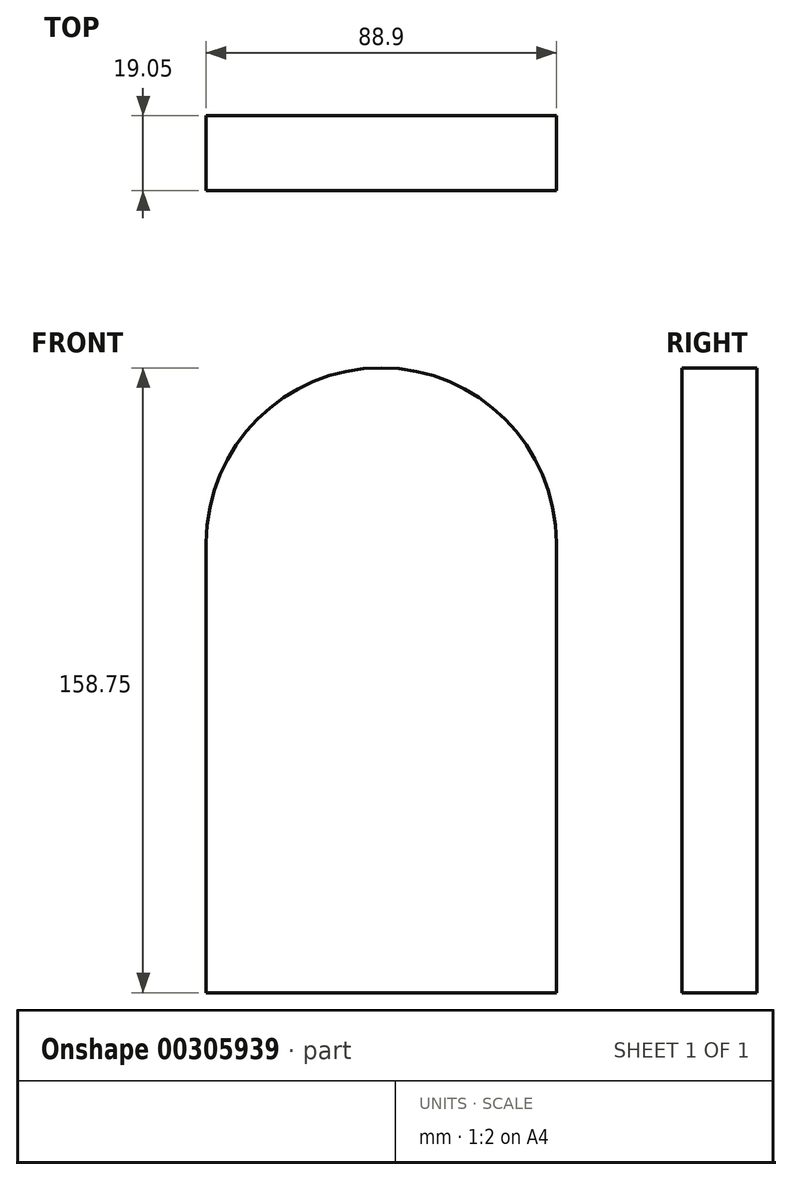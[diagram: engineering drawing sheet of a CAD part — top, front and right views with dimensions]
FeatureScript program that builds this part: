
annotation { "Feature Type Name" : "Feature", "Feature Type Description" : "" }
export const myFeature = defineFeature(function(context is Context, id is Id, definition is map)
    precondition{}
    {
        {
            var Q0;
            Q0=qCreatedBy(makeId("Front.planeOp"),FACE);
            var sketch = newSketch(context, id + "F0", { "sketchPlane" : qUnion([Q0])});
            skLineSegment(sketch, "E0", {"start": v(-44.72, 0) * mm, "end": v(44.18, 0) * mm});
            skLineSegment(sketch, "E1", {"start": v(-44.72, 0) * mm, "end": v(-44.72, 114.3) * mm});
            skLineSegment(sketch, "E2", {"start": v(44.18, 0) * mm, "end": v(44.18, 114.3) * mm});
            skArc(sketch, "E3", {"start": v(44.18, 114.3) * mm, "mid": v(-0.27, 158.75) * mm, "end": v(-44.72, 114.3) * mm});
            skSolve(sketch);
        }
        {
            var Q0;
            Q0=makeQuery(id+"F0.imprint","IMPRINT",FACE,{"disambiguationData":[TD([[makeQuery(id+"F0.imprint","IMPRINT",EDGE,{"derivedFrom":sQuery(id+"F0.wireOp",EDGE,"E0")}),1.0]])]});
            extrude(context, id + "F1", {"entities" : qUnion([Q0]), "depth" : 19.05 * mm});
        }
    });
